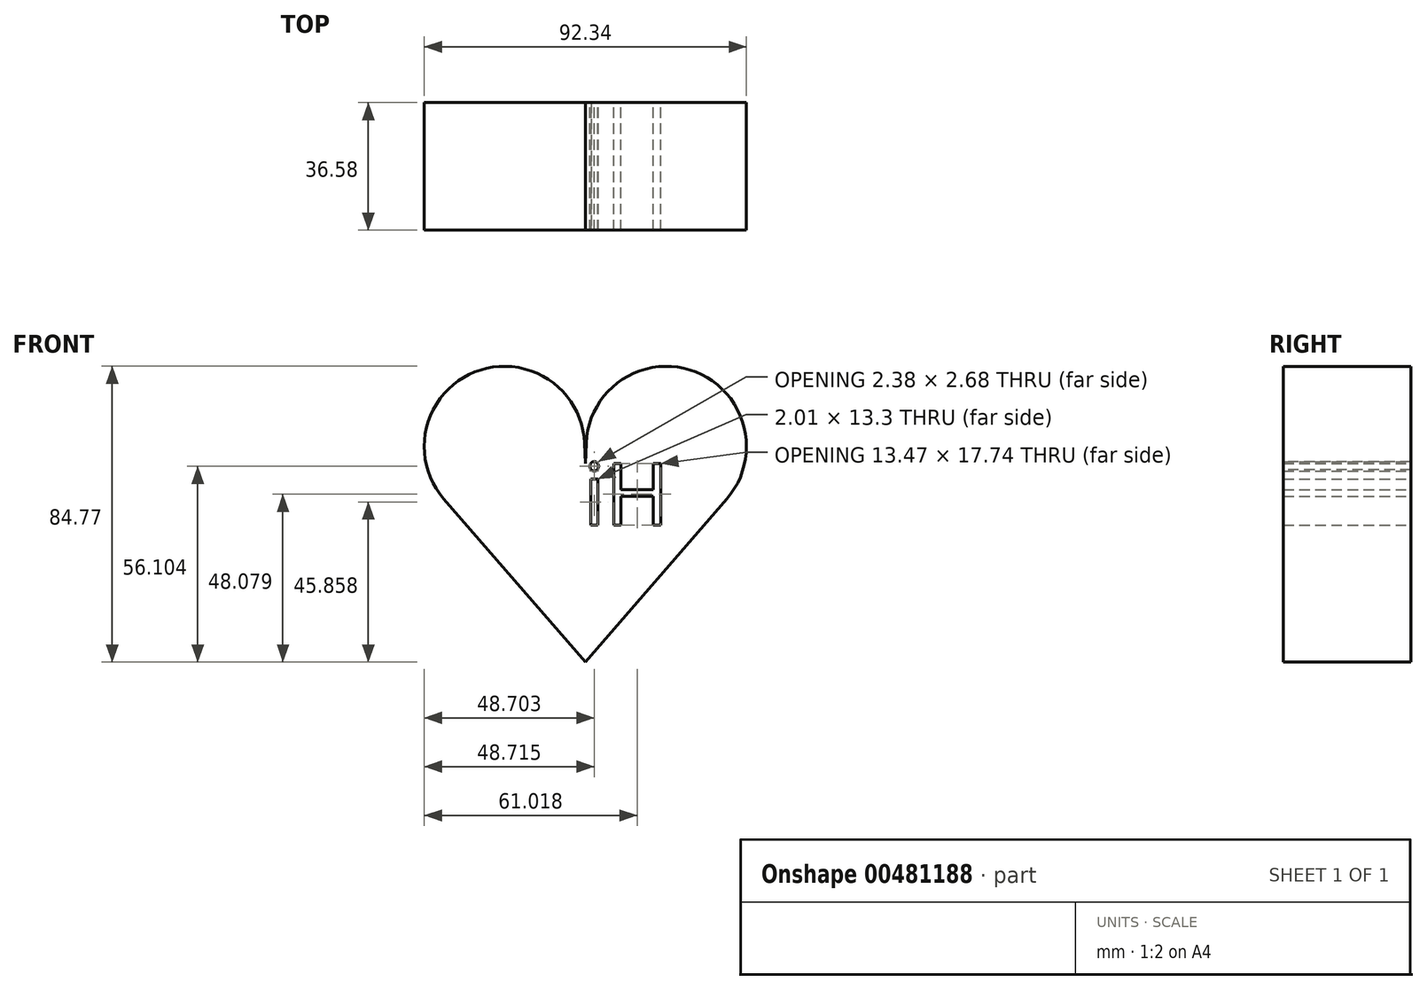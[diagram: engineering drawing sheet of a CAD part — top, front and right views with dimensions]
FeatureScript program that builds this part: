
annotation { "Feature Type Name" : "Feature", "Feature Type Description" : "" }
export const myFeature = defineFeature(function(context is Context, id is Id, definition is map)
    precondition{}
    {
        {
            var Q0;
            Q0=qCreatedBy(makeId("Front.planeOp"),FACE);
            var sketch = newSketch(context, id + "F0", { "sketchPlane" : qUnion([Q0])});
            skLineSegment(sketch, "E0", {"start": v(-40.55, 22.37) * mm, "end": v(0, -24.38) * mm});
            skLineSegment(sketch, "E1.MirrorCS", {"start": v(40.55, 22.37) * mm, "end": v(0, -24.38) * mm});
            skArc(sketch, "E2", {"start": v(-0.26, 38.34) * mm, "mid": v(-31.67, 58.77) * mm, "end": v(-40.55, 22.37) * mm});
            skArc(sketch, "E3", {"start": v(0.26, 38.35) * mm, "mid": v(31.67, 58.77) * mm, "end": v(40.55, 22.37) * mm});
            skLineSegment(sketch, "E4", {"start": v(0.26, 38.35) * mm, "end": v(0.26, 38.35) * mm});
            skLineSegment(sketch, "E5", {"start": v(-0.26, 38.34) * mm, "end": v(-0.02, 32.51) * mm});
            skLineSegment(sketch, "E6", {"start": v(-0.02, 32.51) * mm, "end": v(0.26, 38.35) * mm});
            skSolve(sketch);
        }
        {
            var Q0;
            Q0=makeQuery(id+"F0.imprint","IMPRINT",FACE,{"disambiguationData":[TD([[makeQuery(id+"F0.imprint","IMPRINT",EDGE,{"derivedFrom":sQuery(id+"F0.wireOp",EDGE,"E0")}),1.0]])]});
            var Q1;
            Q1 = qSketchRegion(id + "F0", true);
            extrude(context, id + "F1", {"entities" : qUnion([Q0, Q1]), "depth" : 36.58 * mm});
        }
        {
            var Q0;
            Q0=makeQuery(id+"F1.opExtrude","CAP_FACE",FACE,{"disambiguationData":[OSD([sQuery(id+"F0.wireOp",EDGE,"E0"),sQuery(id+"F0.wireOp",EDGE,"E1.MirrorCS"),sQuery(id+"F0.wireOp",EDGE,"E2"),sQuery(id+"F0.wireOp",EDGE,"E3"),sQuery(id+"F0.wireOp",EDGE,"E5"),sQuery(id+"F0.wireOp",EDGE,"E6")])],"isStart":true});
            var sketch = newSketch(context, id + "F2", { "sketchPlane" : qUnion([Q0])});
            skText(sketch, "E7", { "text": "Hi", "fontName": "OpenSans-Regular.ttf"});
            const initialGuessF2  = {"E7": [-0.02402, 0.01483, 1, 0, 0.01789]};
            skSetInitialGuess(sketch, initialGuessF2);
            skSolve(sketch);
        }
        {
            var Q0;
            Q0 = qSketchRegion(id + "F2", true);
            extrude(context, id + "F3", {"entities" : qUnion([Q0]), "operationType" : NewBodyOperationType.REMOVE, "oppositeDirection" : true, "depth" : 42.42 * mm});
        }
    });
